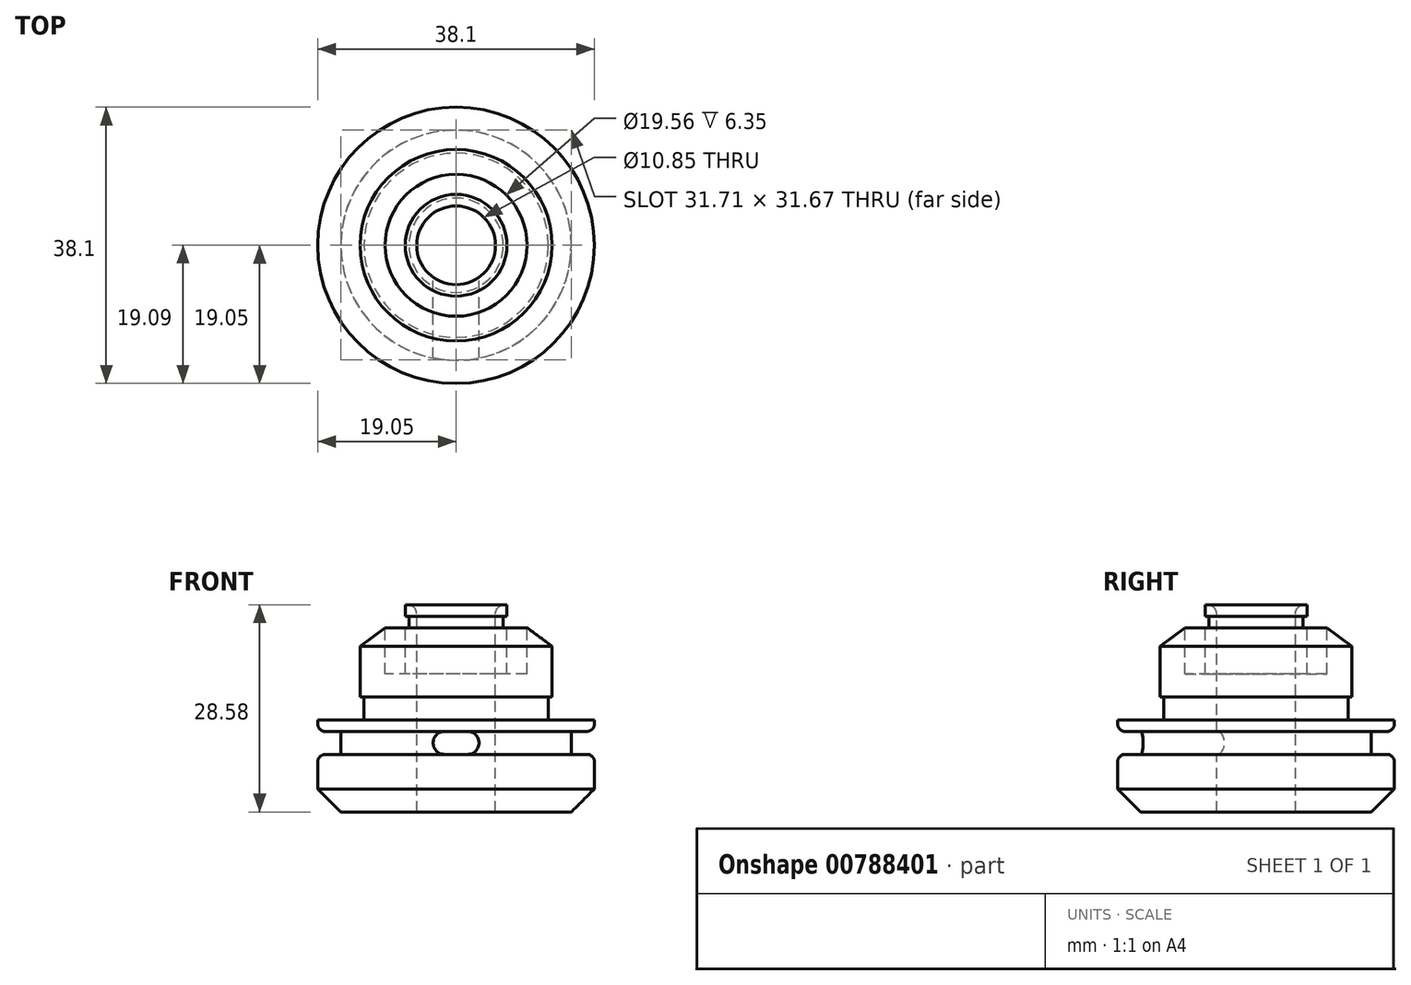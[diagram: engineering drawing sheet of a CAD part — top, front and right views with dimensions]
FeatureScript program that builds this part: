
annotation { "Feature Type Name" : "Feature", "Feature Type Description" : "" }
export const myFeature = defineFeature(function(context is Context, id is Id, definition is map)
    precondition{}
    {
        {
            var Q0;
            Q0=qCreatedBy(makeId("Front.planeOp"),FACE);
            var sketch = newSketch(context, id + "F0", { "sketchPlane" : qUnion([Q0])});
            skLineSegment(sketch, "E0", {"start": v(-5.42, -12.7) * mm, "end": v(-19.05, -12.7) * mm});
            skLineSegment(sketch, "E1", {"start": v(-19.05, -12.7) * mm, "end": v(-19.05, -4.76) * mm});
            skLineSegment(sketch, "E2", {"start": v(-19.05, -4.76) * mm, "end": v(-15.88, -4.76) * mm});
            skLineSegment(sketch, "E3", {"start": v(-15.88, -4.76) * mm, "end": v(-15.88, -1.59) * mm});
            skLineSegment(sketch, "E4", {"start": v(-15.88, -1.59) * mm, "end": v(-19.05, -1.59) * mm});
            skLineSegment(sketch, "E5", {"start": v(-19.05, -1.59) * mm, "end": v(-19.05, 0) * mm});
            skLineSegment(sketch, "E6", {"start": v(-19.05, 0) * mm, "end": v(-12.7, 0) * mm});
            skLineSegment(sketch, "E7", {"start": v(-7.01, 6.35) * mm, "end": v(-7.01, 12.7) * mm});
            skLineSegment(sketch, "E8", {"start": v(-7.01, 12.7) * mm, "end": v(-6.5, 12.7) * mm});
            skLineSegment(sketch, "E9", {"start": v(-6.5, 12.7) * mm, "end": v(-6.5, 14.29) * mm});
            skLineSegment(sketch, "E10", {"start": v(-6.5, 14.29) * mm, "end": v(-7.01, 14.29) * mm});
            skLineSegment(sketch, "E11", {"start": v(-7.01, 14.29) * mm, "end": v(-7.01, 15.87) * mm});
            skLineSegment(sketch, "E12", {"start": v(-7.01, 15.88) * mm, "end": v(-5.42, 15.88) * mm});
            skLineSegment(sketch, "E13", {"start": v(-5.42, 15.87) * mm, "end": v(-5.42, -12.7) * mm});
            skLineSegment(sketch, "E14", {"start": v(-13.2, 6.35) * mm, "end": v(-13.2, 3.18) * mm});
            skLineSegment(sketch, "E15", {"start": v(-13.2, 3.17) * mm, "end": v(-12.7, 3.17) * mm});
            skLineSegment(sketch, "E16", {"start": v(-12.7, 3.17) * mm, "end": v(-12.7, 0) * mm});
            skLineSegment(sketch, "E17", {"start": v(-9.78, 12.7) * mm, "end": v(-9.78, 6.35) * mm});
            skLineSegment(sketch, "E18", {"start": v(-9.78, 6.35) * mm, "end": v(-7.01, 6.35) * mm});
            skLineSegment(sketch, "E19", {"start": v(0, 33.54) * mm, "end": v(0, -22.22) * mm, "construction": true});
            skLineSegment(sketch, "E20", {"start": v(-13.2, 6.35) * mm, "end": v(-13.2, 10.16) * mm});
            skLineSegment(sketch, "E21", {"start": v(-13.2, 10.16) * mm, "end": v(-9.78, 12.7) * mm});
            skSolve(sketch);
        }
        {
            var Q0;
            Q0 = qSketchRegion(id + "F0", true);
            var Q1;
            Q1=sQuery(id+"F0.wireOp",EDGE,"E19");
            revolve(context, id + "F1", {"surfaceOperationType" : NewSurfaceOperationType.NEW, "entities" : qUnion([Q0]), "axis" : qUnion([Q1]), "revolveType" : RevolveType.FULL});
        }
        {
            var Q0;
            Q0=makeQuery(id+"F1.opRevolve","SWEPT_EDGE",EDGE,{"disambiguationData":[OSD([sQuery(id+"F0.wireOp",EDGE,"E0"),sQuery(id+"F0.wireOp",EDGE,"E1")])]});
            chamfer(context, id + "F2", {"entities" : qUnion([Q0]), "width" : 3.17 * mm, "tangentPropagation" : true});
        }
        {
            var Q0;
            Q0=qCreatedBy(makeId("Front.planeOp"),FACE);
            var sketch = newSketch(context, id + "F3", { "sketchPlane" : qUnion([Q0])});
            skLineSegment(sketch, "E22.bottom", {"start": v(1.59, -1.59) * mm, "end": v(-1.59, -1.59) * mm});
            skLineSegment(sketch, "E22.top", {"start": v(1.59, -4.76) * mm, "end": v(-1.59, -4.76) * mm});
            skPoint(sketch, "E22.middle", {"position": v(0, -3.18) * mm});
            skArc(sketch, "E23", {"start": v(1.59, -1.59) * mm, "mid": v(3.17, -3.17) * mm, "end": v(1.59, -4.76) * mm});
            skArc(sketch, "E24", {"start": v(-1.59, -1.59) * mm, "mid": v(-3.17, -3.18) * mm, "end": v(-1.59, -4.76) * mm});
            skSolve(sketch);
        }
        {
            var Q0;
            Q0 = qSketchRegion(id + "F3", true);
            extrude(context, id + "F4", {"entities" : qUnion([Q0]), "operationType" : NewBodyOperationType.REMOVE, "depth" : 25.4 * mm, "offsetDistance" : 25.4 * mm});
        }
        {
            var Q0;
            Q0=makeQuery(id+"F1.opRevolve","SWEPT_EDGE",EDGE,{"disambiguationData":[OSD([sQuery(id+"F0.wireOp",EDGE,"E4"),sQuery(id+"F0.wireOp",EDGE,"E5")])]});
            var Q1;
            Q1=makeQuery(id+"F1.opRevolve","SWEPT_EDGE",EDGE,{"disambiguationData":[OSD([sQuery(id+"F0.wireOp",EDGE,"E1"),sQuery(id+"F0.wireOp",EDGE,"E2")])]});
            fillet(context, id + "F5", {"entities" : qUnion([Q0, Q1]), "radius" : 1.02 * mm, "tangentPropagation" : true, "allowEdgeOverflow" : false});
        }
        {
            var Q0;
            Q0=makeQuery(id+"F1.opRevolve","SWEPT_EDGE",EDGE,{"disambiguationData":[OSD([sQuery(id+"F0.wireOp",EDGE,"E12"),sQuery(id+"F0.wireOp",EDGE,"E13")])]});
            fillet(context, id + "F6", {"entities" : qUnion([Q0]), "radius" : 1.27 * mm, "tangentPropagation" : true, "allowEdgeOverflow" : false});
        }
    });
